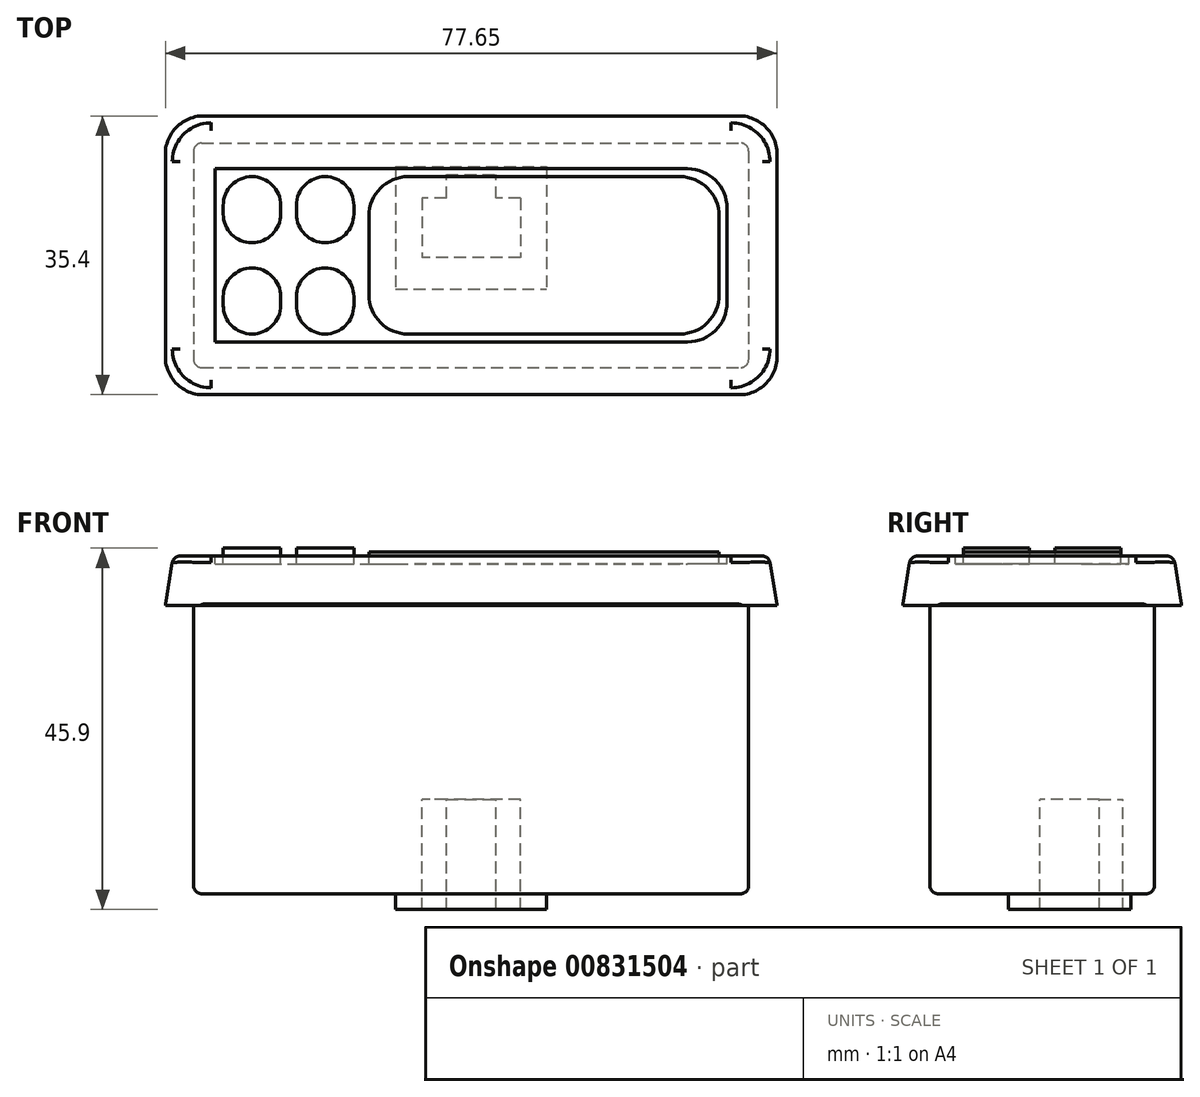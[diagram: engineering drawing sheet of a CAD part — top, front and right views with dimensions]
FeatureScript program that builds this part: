
annotation { "Feature Type Name" : "Feature", "Feature Type Description" : "" }
export const myFeature = defineFeature(function(context is Context, id is Id, definition is map)
    precondition{}
    {
        {
            var Q0;
            Q0=qCreatedBy(makeId("Top.planeOp"),FACE);
            var sketch = newSketch(context, id + "F0", { "sketchPlane" : qUnion([Q0])});
            skLineSegment(sketch, "E0.bottom", {"start": v(0, 0) * mm, "end": v(77.65, 0) * mm});
            skLineSegment(sketch, "E0.top", {"start": v(0, 35.4) * mm, "end": v(77.65, 35.4) * mm});
            skLineSegment(sketch, "E0.left", {"start": v(0, 0) * mm, "end": v(0, 35.4) * mm});
            skLineSegment(sketch, "E0.right", {"start": v(77.65, 0) * mm, "end": v(77.65, 35.4) * mm});
            skSolve(sketch);
        }
        {
            var Q0;
            Q0 = qSketchRegion(id + "F0", true);
            extrude(context, id + "F1", {"entities" : qUnion([Q0]), "depth" : 6.3 * mm, "offsetDistance" : 25 * mm});
        }
        {
            var Q0;
            Q0=makeQuery(id+"F1.opExtrude","CAP_FACE",FACE,{"disambiguationData":[OSD([sQuery(id+"F0.wireOp",EDGE,"E0.bottom"),sQuery(id+"F0.wireOp",EDGE,"E0.top"),sQuery(id+"F0.wireOp",EDGE,"E0.left"),sQuery(id+"F0.wireOp",EDGE,"E0.right")])],"isStart":true});
            var sketch = newSketch(context, id + "F2", { "sketchPlane" : qUnion([Q0])});
            skLineSegment(sketch, "E1.bottom", {"start": v(3.58, -31.95) * mm, "end": v(74.08, -31.95) * mm});
            skLineSegment(sketch, "E1.top", {"start": v(3.57, -3.45) * mm, "end": v(74.08, -3.45) * mm});
            skLineSegment(sketch, "E1.left", {"start": v(3.58, -31.95) * mm, "end": v(3.57, -3.45) * mm});
            skLineSegment(sketch, "E1.right", {"start": v(74.08, -31.95) * mm, "end": v(74.08, -3.45) * mm});
            skSolve(sketch);
        }
        {
            var Q0;
            Q0 = qSketchRegion(id + "F2", true);
            extrude(context, id + "F3", {"entities" : qUnion([Q0]), "operationType" : NewBodyOperationType.ADD, "depth" : 36.6 * mm, "offsetDistance" : 25 * mm});
        }
        {
            var Q0;
            Q0=makeQuery(id+"F3.opExtrude","CAP_FACE",FACE,{"disambiguationData":[OSD([sQuery(id+"F2.wireOp",EDGE,"E1.bottom"),sQuery(id+"F2.wireOp",EDGE,"E1.top"),sQuery(id+"F2.wireOp",EDGE,"E1.left"),sQuery(id+"F2.wireOp",EDGE,"E1.right")])],"isStart":false});
            var sketch = newSketch(context, id + "F4", { "sketchPlane" : qUnion([Q0])});
            skLineSegment(sketch, "E2.bottom", {"start": v(29.23, -28.95) * mm, "end": v(48.43, -28.95) * mm});
            skLineSegment(sketch, "E2.top", {"start": v(29.23, -13.45) * mm, "end": v(48.43, -13.45) * mm});
            skLineSegment(sketch, "E2.left", {"start": v(29.23, -28.95) * mm, "end": v(29.23, -13.45) * mm});
            skLineSegment(sketch, "E2.right", {"start": v(48.43, -28.95) * mm, "end": v(48.43, -13.45) * mm});
            skLineSegment(sketch, "E3.bottom", {"start": v(45.08, -24.95) * mm, "end": v(32.58, -24.95) * mm});
            skLineSegment(sketch, "E3.top", {"start": v(45.08, -17.45) * mm, "end": v(32.58, -17.45) * mm});
            skLineSegment(sketch, "E3.left", {"start": v(45.08, -24.95) * mm, "end": v(45.08, -17.45) * mm});
            skLineSegment(sketch, "E3.right", {"start": v(32.58, -24.95) * mm, "end": v(32.58, -17.45) * mm});
            skPoint(sketch, "E3.middle", {"position": v(38.83, -21.2) * mm});
            skPoint(sketch, "E3.middle.positionSnap0", {"position": v(38.83, -28.95) * mm});
            skPoint(sketch, "E3.middle.positionSnap1", {"position": v(29.23, -21.2) * mm});
            skPoint(sketch, "E3.centerSnap0", {"position": v(38.83, -28.95) * mm});
            skPoint(sketch, "E3.centerSnap1", {"position": v(29.23, -21.2) * mm});
            skLineSegment(sketch, "E4.bottom", {"start": v(35.68, -24.95) * mm, "end": v(41.98, -24.95) * mm});
            skLineSegment(sketch, "E4.top", {"start": v(35.68, -27.95) * mm, "end": v(41.98, -27.95) * mm});
            skLineSegment(sketch, "E4.left", {"start": v(35.68, -24.95) * mm, "end": v(35.68, -27.95) * mm});
            skLineSegment(sketch, "E4.right", {"start": v(41.98, -24.95) * mm, "end": v(41.98, -27.95) * mm});
            skSolve(sketch);
        }
        {
            var Q0;
            Q0=makeQuery(id+"F4.imprint","IMPRINT",FACE,{"disambiguationData":[TD([[makeQuery(id+"F4.imprint","IMPRINT",EDGE,{"derivedFrom":sQuery(id+"F4.wireOp",EDGE,"E2.bottom")}),1.0]])]});
            extrude(context, id + "F5", {"entities" : qUnion([Q0]), "operationType" : NewBodyOperationType.ADD, "depth" : 2 * mm, "offsetDistance" : 25 * mm});
        }
        {
            var Q0;
            Q0=makeQuery(id+"F5.boolean.opBoolean","SPLIT",FACE,{"disambiguationData":[TD([makeQuery(id+"F5.opExtrude","SWEPT_FACE",FACE,{"disambiguationData":[OSD([sQuery(id+"F4.wireOp",EDGE,"E3.top")])]})])],"derivedFrom":makeQuery(id+"F3.opExtrude","CAP_FACE",FACE,{"disambiguationData":[OSD([sQuery(id+"F2.wireOp",EDGE,"E1.bottom"),sQuery(id+"F2.wireOp",EDGE,"E1.top"),sQuery(id+"F2.wireOp",EDGE,"E1.left"),sQuery(id+"F2.wireOp",EDGE,"E1.right")])],"isStart":false})});
            extrude(context, id + "F6", {"entities" : qUnion([Q0]), "operationType" : NewBodyOperationType.REMOVE, "oppositeDirection" : true, "depth" : 12 * mm, "offsetDistance" : 25 * mm});
        }
        {
            var Q0;
            Q0=makeQuery(id+"F1.opExtrude","CAP_FACE",FACE,{"disambiguationData":[OSD([sQuery(id+"F0.wireOp",EDGE,"E0.bottom"),sQuery(id+"F0.wireOp",EDGE,"E0.top"),sQuery(id+"F0.wireOp",EDGE,"E0.left"),sQuery(id+"F0.wireOp",EDGE,"E0.right")])],"isStart":false});
            var sketch = newSketch(context, id + "F7", { "sketchPlane" : qUnion([Q0])});
            skLineSegment(sketch, "E5.bottom", {"start": v(6.33, 28.7) * mm, "end": v(71.33, 28.7) * mm});
            skLineSegment(sketch, "E5.top", {"start": v(6.33, 6.7) * mm, "end": v(71.33, 6.7) * mm});
            skLineSegment(sketch, "E5.left", {"start": v(6.33, 28.7) * mm, "end": v(6.33, 6.7) * mm});
            skLineSegment(sketch, "E5.right", {"start": v(71.33, 28.7) * mm, "end": v(71.33, 6.7) * mm});
            skPoint(sketch, "E5.middle", {"position": v(38.83, 17.7) * mm});
            skPoint(sketch, "E5.middle.positionSnap0", {"position": v(0, 17.7) * mm});
            skPoint(sketch, "E5.middle.positionSnap1", {"position": v(38.83, 35.4) * mm});
            skPoint(sketch, "E5.centerSnap0", {"position": v(0, 17.7) * mm});
            skPoint(sketch, "E5.centerSnap1", {"position": v(38.83, 35.4) * mm});
            skLineSegment(sketch, "E6.bottom", {"start": v(70.33, 27.7) * mm, "end": v(25.83, 27.7) * mm});
            skLineSegment(sketch, "E6.top", {"start": v(70.33, 7.7) * mm, "end": v(25.82, 7.7) * mm});
            skLineSegment(sketch, "E6.left", {"start": v(70.33, 27.7) * mm, "end": v(70.33, 7.7) * mm});
            skLineSegment(sketch, "E6.right", {"start": v(25.82, 27.7) * mm, "end": v(25.83, 7.7) * mm});
            skArc(sketch, "E7", {"start": v(7.33, 11.35) * mm, "mid": v(10.98, 7.7) * mm, "end": v(14.63, 11.35) * mm});
            skLineSegment(sketch, "E8", {"start": v(7.33, 11.35) * mm, "end": v(7.33, 11.9) * mm});
            skLineSegment(sketch, "E9", {"start": v(14.63, 11.35) * mm, "end": v(14.63, 11.9) * mm});
            skLineSegment(sketch, "E10", {"start": v(14.63, 11.9) * mm, "end": v(7.33, 11.9) * mm});
            skArc(sketch, "E11.MirrorCS", {"start": v(7.33, 12.45) * mm, "mid": v(10.98, 16.1) * mm, "end": v(14.63, 12.45) * mm});
            skLineSegment(sketch, "E12.MirrorCS", {"start": v(7.33, 12.45) * mm, "end": v(7.33, 11.9) * mm});
            skLineSegment(sketch, "E13.MirrorCS", {"start": v(14.63, 12.45) * mm, "end": v(14.63, 11.9) * mm});
            skLineSegment(sketch, "E14.MirrorCS", {"start": v(7.33, 24.05) * mm, "end": v(7.33, 23.5) * mm});
            skLineSegment(sketch, "E15.MirrorCS", {"start": v(14.63, 24.05) * mm, "end": v(14.63, 23.5) * mm});
            skLineSegment(sketch, "E16.MirrorCS", {"start": v(7.33, 22.95) * mm, "end": v(7.33, 23.5) * mm});
            skLineSegment(sketch, "E17.MirrorCS", {"start": v(14.63, 22.95) * mm, "end": v(14.63, 23.5) * mm});
            skArc(sketch, "E18.MirrorCS", {"start": v(7.33, 22.95) * mm, "mid": v(10.98, 19.3) * mm, "end": v(14.63, 22.95) * mm});
            skLineSegment(sketch, "E19.MirrorCS", {"start": v(14.63, 23.5) * mm, "end": v(7.33, 23.5) * mm});
            skArc(sketch, "E20.MirrorCS", {"start": v(7.33, 24.05) * mm, "mid": v(10.98, 27.7) * mm, "end": v(14.63, 24.05) * mm});
            skLineSegment(sketch, "E21.MirrorCS", {"start": v(23.93, 24.05) * mm, "end": v(23.93, 23.5) * mm});
            skLineSegment(sketch, "E22.MirrorCS", {"start": v(23.93, 22.95) * mm, "end": v(23.93, 23.5) * mm});
            skLineSegment(sketch, "E23.MirrorCS", {"start": v(23.93, 12.45) * mm, "end": v(23.93, 11.9) * mm});
            skLineSegment(sketch, "E24.MirrorCS", {"start": v(23.93, 11.35) * mm, "end": v(23.93, 11.9) * mm});
            skLineSegment(sketch, "E25.MirrorCS", {"start": v(16.63, 24.05) * mm, "end": v(16.63, 23.5) * mm});
            skArc(sketch, "E26.MirrorCS", {"start": v(23.93, 11.35) * mm, "mid": v(20.28, 7.7) * mm, "end": v(16.62, 11.35) * mm});
            skLineSegment(sketch, "E27.MirrorCS", {"start": v(16.62, 22.95) * mm, "end": v(16.62, 23.5) * mm});
            skLineSegment(sketch, "E28.MirrorCS", {"start": v(16.63, 11.9) * mm, "end": v(23.93, 11.9) * mm});
            skLineSegment(sketch, "E29.MirrorCS", {"start": v(16.62, 12.45) * mm, "end": v(16.62, 11.9) * mm});
            skArc(sketch, "E30.MirrorCS", {"start": v(23.93, 22.95) * mm, "mid": v(20.28, 19.3) * mm, "end": v(16.62, 22.95) * mm});
            skLineSegment(sketch, "E31.MirrorCS", {"start": v(16.63, 23.5) * mm, "end": v(23.93, 23.5) * mm});
            skArc(sketch, "E32.MirrorCS", {"start": v(23.93, 24.05) * mm, "mid": v(20.28, 27.7) * mm, "end": v(16.62, 24.05) * mm});
            skArc(sketch, "E33.MirrorCS", {"start": v(23.93, 12.45) * mm, "mid": v(20.28, 16.1) * mm, "end": v(16.62, 12.45) * mm});
            skLineSegment(sketch, "E34.MirrorCS", {"start": v(16.63, 11.35) * mm, "end": v(16.63, 11.9) * mm});
            skSolve(sketch);
        }
        {
            var Q0;
            Q0 = qSketchRegion(id + "F7", true);
            extrude(context, id + "F8", {"entities" : qUnion([Q0]), "operationType" : NewBodyOperationType.REMOVE, "oppositeDirection" : true, "depth" : 1 * mm, "offsetDistance" : 25 * mm});
        }
        {
            var Q0;
            Q0=makeQuery(id+"F8.boolean.opBoolean","SPLIT",FACE,{"disambiguationData":[TD([makeQuery(id+"F8.opExtrude","SWEPT_FACE",FACE,{"disambiguationData":[OSD([sQuery(id+"F7.wireOp",EDGE,"E26.MirrorCS")])]})])],"derivedFrom":makeQuery(id+"F1.opExtrude","CAP_FACE",FACE,{"disambiguationData":[OSD([sQuery(id+"F0.wireOp",EDGE,"E0.bottom"),sQuery(id+"F0.wireOp",EDGE,"E0.top"),sQuery(id+"F0.wireOp",EDGE,"E0.left"),sQuery(id+"F0.wireOp",EDGE,"E0.right")])],"isStart":false})});
            var Q1;
            Q1=makeQuery(id+"F8.boolean.opBoolean","SPLIT",FACE,{"disambiguationData":[TD([makeQuery(id+"F8.opExtrude","SWEPT_FACE",FACE,{"disambiguationData":[OSD([sQuery(id+"F7.wireOp",EDGE,"E7")])]})])],"derivedFrom":makeQuery(id+"F1.opExtrude","CAP_FACE",FACE,{"disambiguationData":[OSD([sQuery(id+"F0.wireOp",EDGE,"E0.bottom"),sQuery(id+"F0.wireOp",EDGE,"E0.top"),sQuery(id+"F0.wireOp",EDGE,"E0.left"),sQuery(id+"F0.wireOp",EDGE,"E0.right")])],"isStart":false})});
            var Q2;
            Q2=makeQuery(id+"F8.boolean.opBoolean","SPLIT",FACE,{"disambiguationData":[TD([makeQuery(id+"F8.opExtrude","SWEPT_FACE",FACE,{"disambiguationData":[OSD([sQuery(id+"F7.wireOp",EDGE,"E18.MirrorCS")])]})])],"derivedFrom":makeQuery(id+"F1.opExtrude","CAP_FACE",FACE,{"disambiguationData":[OSD([sQuery(id+"F0.wireOp",EDGE,"E0.bottom"),sQuery(id+"F0.wireOp",EDGE,"E0.top"),sQuery(id+"F0.wireOp",EDGE,"E0.left"),sQuery(id+"F0.wireOp",EDGE,"E0.right")])],"isStart":false})});
            var Q3;
            Q3=makeQuery(id+"F8.boolean.opBoolean","SPLIT",FACE,{"disambiguationData":[TD([makeQuery(id+"F8.opExtrude","SWEPT_FACE",FACE,{"disambiguationData":[OSD([sQuery(id+"F7.wireOp",EDGE,"E30.MirrorCS")])]})])],"derivedFrom":makeQuery(id+"F1.opExtrude","CAP_FACE",FACE,{"disambiguationData":[OSD([sQuery(id+"F0.wireOp",EDGE,"E0.bottom"),sQuery(id+"F0.wireOp",EDGE,"E0.top"),sQuery(id+"F0.wireOp",EDGE,"E0.left"),sQuery(id+"F0.wireOp",EDGE,"E0.right")])],"isStart":false})});
            extrude(context, id + "F9", {"entities" : qUnion([Q0, Q1, Q2, Q3]), "depth" : 1 * mm, "offsetDistance" : 25 * mm});
        }
        {
            var Q0;
            Q0=makeQuery(id+"F8.boolean.opBoolean","SPLIT",FACE,{"disambiguationData":[TD([makeQuery(id+"F8.opExtrude","SWEPT_FACE",FACE,{"disambiguationData":[OSD([sQuery(id+"F7.wireOp",EDGE,"E6.bottom")])]})])],"derivedFrom":makeQuery(id+"F1.opExtrude","CAP_FACE",FACE,{"disambiguationData":[OSD([sQuery(id+"F0.wireOp",EDGE,"E0.bottom"),sQuery(id+"F0.wireOp",EDGE,"E0.top"),sQuery(id+"F0.wireOp",EDGE,"E0.left"),sQuery(id+"F0.wireOp",EDGE,"E0.right")])],"isStart":false})});
            extrude(context, id + "F10", {"entities" : qUnion([Q0]), "depth" : .5 * mm, "offsetDistance" : 25 * mm});
        }
        {
            var Q0;
            Q0=makeQuery(id+"F1.opExtrude","CAP_EDGE",EDGE,{"disambiguationData":[OSD([sQuery(id+"F0.wireOp",EDGE,"E0.right")])],"isStart":false});
            var Q1;
            Q1=makeQuery(id+"F1.opExtrude","CAP_EDGE",EDGE,{"disambiguationData":[OSD([sQuery(id+"F0.wireOp",EDGE,"E0.top")])],"isStart":false});
            var Q2;
            Q2=makeQuery(id+"F1.opExtrude","CAP_EDGE",EDGE,{"disambiguationData":[OSD([sQuery(id+"F0.wireOp",EDGE,"E0.left")])],"isStart":false});
            var Q3;
            Q3=makeQuery(id+"F1.opExtrude","CAP_EDGE",EDGE,{"disambiguationData":[OSD([sQuery(id+"F0.wireOp",EDGE,"E0.bottom")])],"isStart":false});
            chamfer(context, id + "F11", {"entities" : qUnion([Q0, Q1, Q2, Q3]), "chamferType" : ChamferType.TWO_OFFSETS, "width1" : 1 * mm, "oppositeDirection" : false, "width2" : 6.1 * mm, "tangentPropagation" : true});
        }
        {
            var Q0;
            Q0=makeQuery(id+"F11.opChamfer","BLEND_EDGE",EDGE,{"blendedFrom":[makeQuery(id+"F1.opExtrude","CAP_EDGE",EDGE,{"disambiguationData":[OSD([sQuery(id+"F0.wireOp",EDGE,"E0.bottom")])],"isStart":false}),makeQuery(id+"F1.opExtrude","CAP_EDGE",EDGE,{"disambiguationData":[OSD([sQuery(id+"F0.wireOp",EDGE,"E0.left")])],"isStart":false})],"blendedInto":[]});
            var Q1;
            Q1=makeQuery(id+"F11.opChamfer","BLEND_EDGE",EDGE,{"blendedFrom":[makeQuery(id+"F1.opExtrude","CAP_EDGE",EDGE,{"disambiguationData":[OSD([sQuery(id+"F0.wireOp",EDGE,"E0.bottom")])],"isStart":false}),makeQuery(id+"F1.opExtrude","CAP_EDGE",EDGE,{"disambiguationData":[OSD([sQuery(id+"F0.wireOp",EDGE,"E0.right")])],"isStart":false})],"blendedInto":[]});
            var Q2;
            Q2=makeQuery(id+"F11.opChamfer","BLEND_EDGE",EDGE,{"blendedFrom":[makeQuery(id+"F1.opExtrude","CAP_EDGE",EDGE,{"disambiguationData":[OSD([sQuery(id+"F0.wireOp",EDGE,"E0.top")])],"isStart":false}),makeQuery(id+"F1.opExtrude","CAP_EDGE",EDGE,{"disambiguationData":[OSD([sQuery(id+"F0.wireOp",EDGE,"E0.right")])],"isStart":false})],"blendedInto":[]});
            var Q3;
            Q3=makeQuery(id+"F11.opChamfer","BLEND_EDGE",EDGE,{"blendedFrom":[makeQuery(id+"F1.opExtrude","CAP_EDGE",EDGE,{"disambiguationData":[OSD([sQuery(id+"F0.wireOp",EDGE,"E0.top")])],"isStart":false}),makeQuery(id+"F1.opExtrude","CAP_EDGE",EDGE,{"disambiguationData":[OSD([sQuery(id+"F0.wireOp",EDGE,"E0.left")])],"isStart":false})],"blendedInto":[]});
            fillet(context, id + "F12", {"entities" : qUnion([Q0, Q1, Q2, Q3]), "radius" : 5 * mm, "tangentPropagation" : true, "allowEdgeOverflow" : false});
        }
        {
            var Q0;
            {var subQ0=sQuery(id+"F0.wireOp",EDGE,"E0.left");var subQ1=sQuery(id+"F0.wireOp",EDGE,"E0.top");var subQ2=sQuery(id+"F0.wireOp",EDGE,"E0.right");var subQ3=sQuery(id+"F0.wireOp",EDGE,"E0.bottom");Q0=makeQuery(id+"F11.opChamfer","BLEND_EDGE",EDGE,{"blendedFrom":[makeQuery(id+"F1.opExtrude","CAP_EDGE",EDGE,{"disambiguationData":[OSD([subQ1])],"isStart":false}),makeQuery(id+"F8.boolean.opBoolean","SPLIT",FACE,{"disambiguationData":[TD([makeQuery(id+"F1.opExtrude","SWEPT_FACE",FACE,{"disambiguationData":[OSD([subQ3])]})])],"derivedFrom":makeQuery(id+"F1.opExtrude","CAP_FACE",FACE,{"disambiguationData":[OSD([subQ3,subQ1,subQ0,subQ2])],"isStart":false})})],"blendedInto":[makeQuery(id+"F8.boolean.opBoolean","SPLIT",FACE,{"disambiguationData":[TD([makeQuery(id+"F1.opExtrude","SWEPT_FACE",FACE,{"disambiguationData":[OSD([subQ3])]})])],"derivedFrom":makeQuery(id+"F1.opExtrude","CAP_FACE",FACE,{"disambiguationData":[OSD([subQ3,subQ1,subQ0,subQ2])],"isStart":false})})]});}
            var Q1;
            Q1=makeQuery(id+"F3.opExtrude","SWEPT_EDGE",EDGE,{"disambiguationData":[OSD([sQuery(id+"F2.wireOp",EDGE,"E1.top"),sQuery(id+"F2.wireOp",EDGE,"E1.left")])]});
            var Q2;
            Q2=makeQuery(id+"F3.opExtrude","SWEPT_EDGE",EDGE,{"disambiguationData":[OSD([sQuery(id+"F2.wireOp",EDGE,"E1.bottom"),sQuery(id+"F2.wireOp",EDGE,"E1.left")])]});
            var Q3;
            Q3=makeQuery(id+"F3.opExtrude","SWEPT_EDGE",EDGE,{"disambiguationData":[OSD([sQuery(id+"F2.wireOp",EDGE,"E1.bottom"),sQuery(id+"F2.wireOp",EDGE,"E1.right")])]});
            var Q4;
            Q4=makeQuery(id+"F3.opExtrude","SWEPT_EDGE",EDGE,{"disambiguationData":[OSD([sQuery(id+"F2.wireOp",EDGE,"E1.top"),sQuery(id+"F2.wireOp",EDGE,"E1.right")])]});
            var Q5;
            Q5=makeQuery(id+"F3.opExtrude","CAP_EDGE",EDGE,{"disambiguationData":[OSD([sQuery(id+"F2.wireOp",EDGE,"E1.right")])],"isStart":false});
            var Q6;
            Q6=makeQuery(id+"F3.opExtrude","CAP_EDGE",EDGE,{"disambiguationData":[OSD([sQuery(id+"F2.wireOp",EDGE,"E1.top")])],"isStart":false});
            var Q7;
            Q7=makeQuery(id+"F3.opExtrude","CAP_EDGE",EDGE,{"disambiguationData":[OSD([sQuery(id+"F2.wireOp",EDGE,"E1.left")])],"isStart":false});
            var Q8;
            Q8=makeQuery(id+"F3.opExtrude","CAP_EDGE",EDGE,{"disambiguationData":[OSD([sQuery(id+"F2.wireOp",EDGE,"E1.bottom")])],"isStart":false});
            fillet(context, id + "F13", {"entities" : qUnion([Q0, Q1, Q2, Q3, Q4, Q5, Q6, Q7, Q8]), "radius" : 1 * mm, "tangentPropagation" : true, "allowEdgeOverflow" : false});
        }
        {
            var Q0;
            Q0=makeQuery(id+"F8.boolean.opBoolean","COPY",EDGE,{"derivedFrom":makeQuery(id+"F8.opExtrude","SWEPT_EDGE",EDGE,{"disambiguationData":[OSD([sQuery(id+"F7.wireOp",EDGE,"E6.top"),sQuery(id+"F7.wireOp",EDGE,"E6.right")])]})});
            var Q1;
            Q1=makeQuery(id+"F10.opExtrude","SWEPT_EDGE",EDGE,{"disambiguationData":[OSD([sQuery(id+"F7.wireOp",EDGE,"E6.top"),sQuery(id+"F7.wireOp",EDGE,"E6.right")])]});
            var Q2;
            Q2=makeQuery(id+"F10.opExtrude","SWEPT_EDGE",EDGE,{"disambiguationData":[OSD([sQuery(id+"F7.wireOp",EDGE,"E6.bottom"),sQuery(id+"F7.wireOp",EDGE,"E6.right")])]});
            var Q3;
            Q3=makeQuery(id+"F8.boolean.opBoolean","COPY",EDGE,{"derivedFrom":makeQuery(id+"F8.opExtrude","SWEPT_EDGE",EDGE,{"disambiguationData":[OSD([sQuery(id+"F7.wireOp",EDGE,"E6.bottom"),sQuery(id+"F7.wireOp",EDGE,"E6.right")])]})});
            var Q4;
            Q4=makeQuery(id+"F8.boolean.opBoolean","COPY",EDGE,{"derivedFrom":makeQuery(id+"F8.opExtrude","SWEPT_EDGE",EDGE,{"disambiguationData":[OSD([sQuery(id+"F7.wireOp",EDGE,"E6.bottom"),sQuery(id+"F7.wireOp",EDGE,"E6.left")])]})});
            var Q5;
            Q5=makeQuery(id+"F10.opExtrude","SWEPT_EDGE",EDGE,{"disambiguationData":[OSD([sQuery(id+"F7.wireOp",EDGE,"E6.bottom"),sQuery(id+"F7.wireOp",EDGE,"E6.left")])]});
            var Q6;
            Q6=makeQuery(id+"F8.boolean.opBoolean","COPY",EDGE,{"derivedFrom":makeQuery(id+"F8.opExtrude","SWEPT_EDGE",EDGE,{"disambiguationData":[OSD([sQuery(id+"F7.wireOp",EDGE,"E6.top"),sQuery(id+"F7.wireOp",EDGE,"E6.left")])]})});
            var Q7;
            Q7=makeQuery(id+"F10.opExtrude","SWEPT_EDGE",EDGE,{"disambiguationData":[OSD([sQuery(id+"F7.wireOp",EDGE,"E6.top"),sQuery(id+"F7.wireOp",EDGE,"E6.left")])]});
            var Q8;
            Q8=makeQuery(id+"F8.boolean.opBoolean","COPY",EDGE,{"derivedFrom":makeQuery(id+"F8.opExtrude","SWEPT_EDGE",EDGE,{"disambiguationData":[OSD([sQuery(id+"F7.wireOp",EDGE,"E5.top"),sQuery(id+"F7.wireOp",EDGE,"E5.right")])]})});
            var Q9;
            Q9=makeQuery(id+"F8.boolean.opBoolean","COPY",EDGE,{"derivedFrom":makeQuery(id+"F8.opExtrude","SWEPT_EDGE",EDGE,{"disambiguationData":[OSD([sQuery(id+"F7.wireOp",EDGE,"E5.bottom"),sQuery(id+"F7.wireOp",EDGE,"E5.right")])]})});
            fillet(context, id + "F14", {"entities" : qUnion([Q0, Q1, Q2, Q3, Q4, Q5, Q6, Q7, Q8, Q9]), "radius" : 5 * mm, "tangentPropagation" : true, "allowEdgeOverflow" : false});
        }
    });
